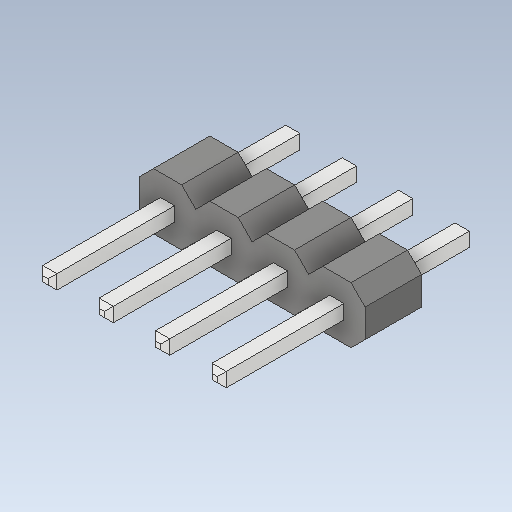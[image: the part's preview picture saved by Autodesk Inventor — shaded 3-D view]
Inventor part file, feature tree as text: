
AUTODESK INVENTOR PART (.ipt)
format: ipt  version: 2020 (Build 240168000, 168)  size: 159,744 bytes
history: imported  units: in
note: dims shown in document units (in); Inventor stores cm internally (conversion verified against a paired STEP export)
features: imported_body x1
ambient origin geometry x8: Origin, YZ Plane, XZ Plane, XY Plane, X Axis, Y Axis, Z Axis, Center Point
bodies: Solid1 (imported_parasolid), Body2 (imported_parasolid)
feature tree (1):
  imported_body  NMx_Import_Brep_tag  [imported B-rep: ~100 faces, bbox_mm=[10.16, 2.54, 11.34]]
